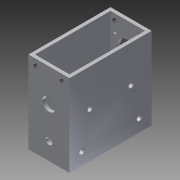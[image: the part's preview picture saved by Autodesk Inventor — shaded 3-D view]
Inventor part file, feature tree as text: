
AUTODESK INVENTOR PART (.ipt)
format: ipt  version: 2013 (Build 170138000, 138)  size: 203,264 bytes
history: native  units: mm
features: sketch x7, hole x5, thread x4, extrude x2, other x1
ambient origin geometry x1: Origin
feature tree (19):
  other  "ソリッド1"
  extrude  "押し出し1"  Depth=25.0mm
  extrude  "押し出し2"  Depth=50.0mm
  hole  "穴1"  [1 undecoded]
  hole  "穴2"  [1 undecoded]
  hole  "穴4"  [1 undecoded]
  thread  "ねじ1"
  thread  "ねじ2"
  thread  "ねじ3"
  thread  "ねじ4"
  hole  "穴5"  [1 undecoded]
  hole  "穴7"  [1 undecoded]
  sketch  "スケッチ1"
  sketch  "スケッチ2"
  sketch  "スケッチ3"
  sketch  "スケッチ4"
  sketch  "スケッチ5"
  sketch  "スケッチ7"
  sketch  "スケッチ8"
note: 5 required parameter values undecoded (feature->parameter linkage not recoverable at this tier; creation-order binding heuristic only, values carry confidence <= 0.55)
